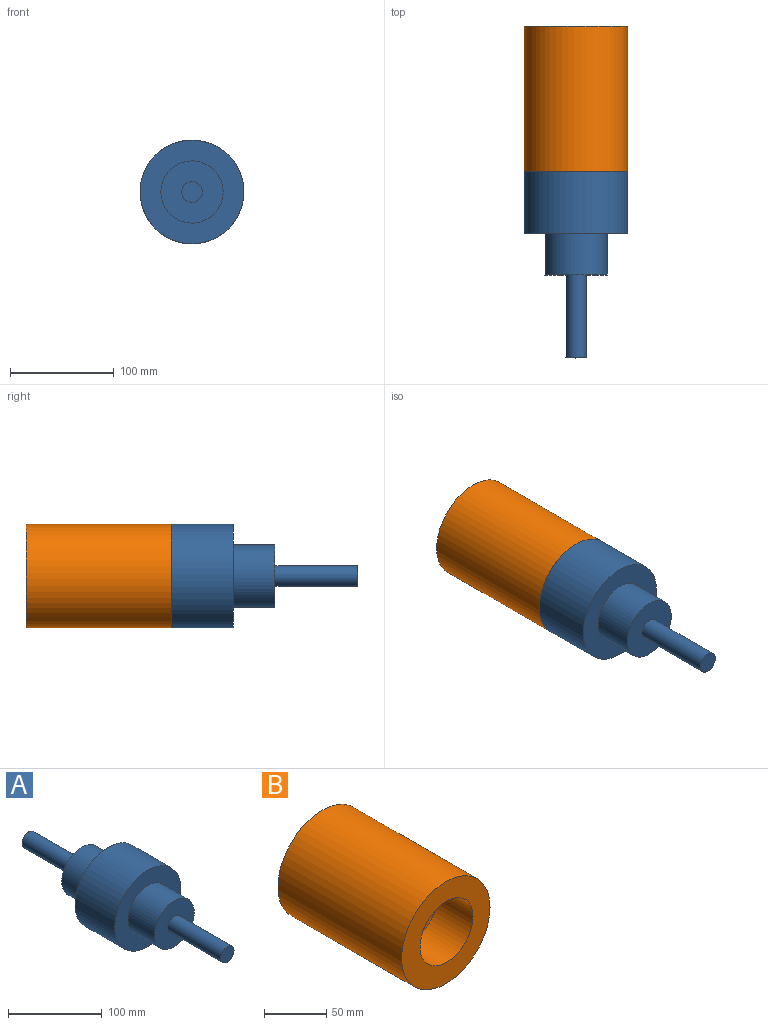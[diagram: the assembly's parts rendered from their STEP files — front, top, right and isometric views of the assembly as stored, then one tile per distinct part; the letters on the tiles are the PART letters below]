
ASSEMBLY  parts=2 mates=1
PART A: 11 faces, bbox 100x300x100 mm
  f0: cylinder r=50mm len=100mm, axis (0,1,0), area 18849.6mm2, adj f1,f2
  f1: plane 100x100mm, normal (0,-1,0), area 5026.5mm2, adj f0,f3
  f2: plane 100x100mm, normal (0,1,0), area 5026.5mm2, adj f0,f7
  f3: cylinder r=30mm len=60mm, axis (0,1,0), area 7539.8mm2, adj f1,f4
  f4: plane 60x60mm, normal (0,-1,0), area 2513.3mm2, adj f3,f5
  f5: cylinder r=10mm len=80mm, axis (0,1,0), area 5026.5mm2, adj f4,f6
  f6: plane 20x20mm, normal (0,-1,0), area 314.2mm2, adj f5
  f7: cylinder r=30mm len=60mm, axis (0,-1,0), area 7539.8mm2, adj f2,f8
  f8: plane 60x60mm, normal (0,1,0), area 2513.3mm2, adj f7,f9
  f9: cylinder r=10mm len=80mm, axis (0,-1,0), area 5026.5mm2, adj f8,f10
  f10: plane 20x20mm, normal (0,1,0), area 314.2mm2, adj f9
PART B: 7 faces, bbox 100x140x100 mm
  f0: cylinder r=50mm len=140mm, axis (0,1,0), area 43982.3mm2, adj f1,f2
  f1: plane 100x100mm, normal (0,-1,0), area 5026.5mm2, adj f0,f3
  f2: plane 100x100mm, normal (0,1,0), area 7854mm2, adj f0
  f3: cylinder r=30mm len=60mm, axis (0,-1,0), area 7539.8mm2, adj f1,f4
  f4: plane 60x60mm, normal (0,-1,0), area 2513.3mm2, adj f3,f5
  f5: cylinder r=10mm len=80mm, axis (0,-1,0), area 5026.5mm2, adj f4,f6
  f6: plane 20x20mm, normal (0,-1,0), area 314.2mm2, adj f5
PLACE A t=(-134.32,82.98,12.14)mm
PLACE B t=(-134.32,222.98,12.14)mm
MATE fastened B.f0 <-> A.f0  axis (0,-1,0) through (-134.32,82.98,12.14)mm
